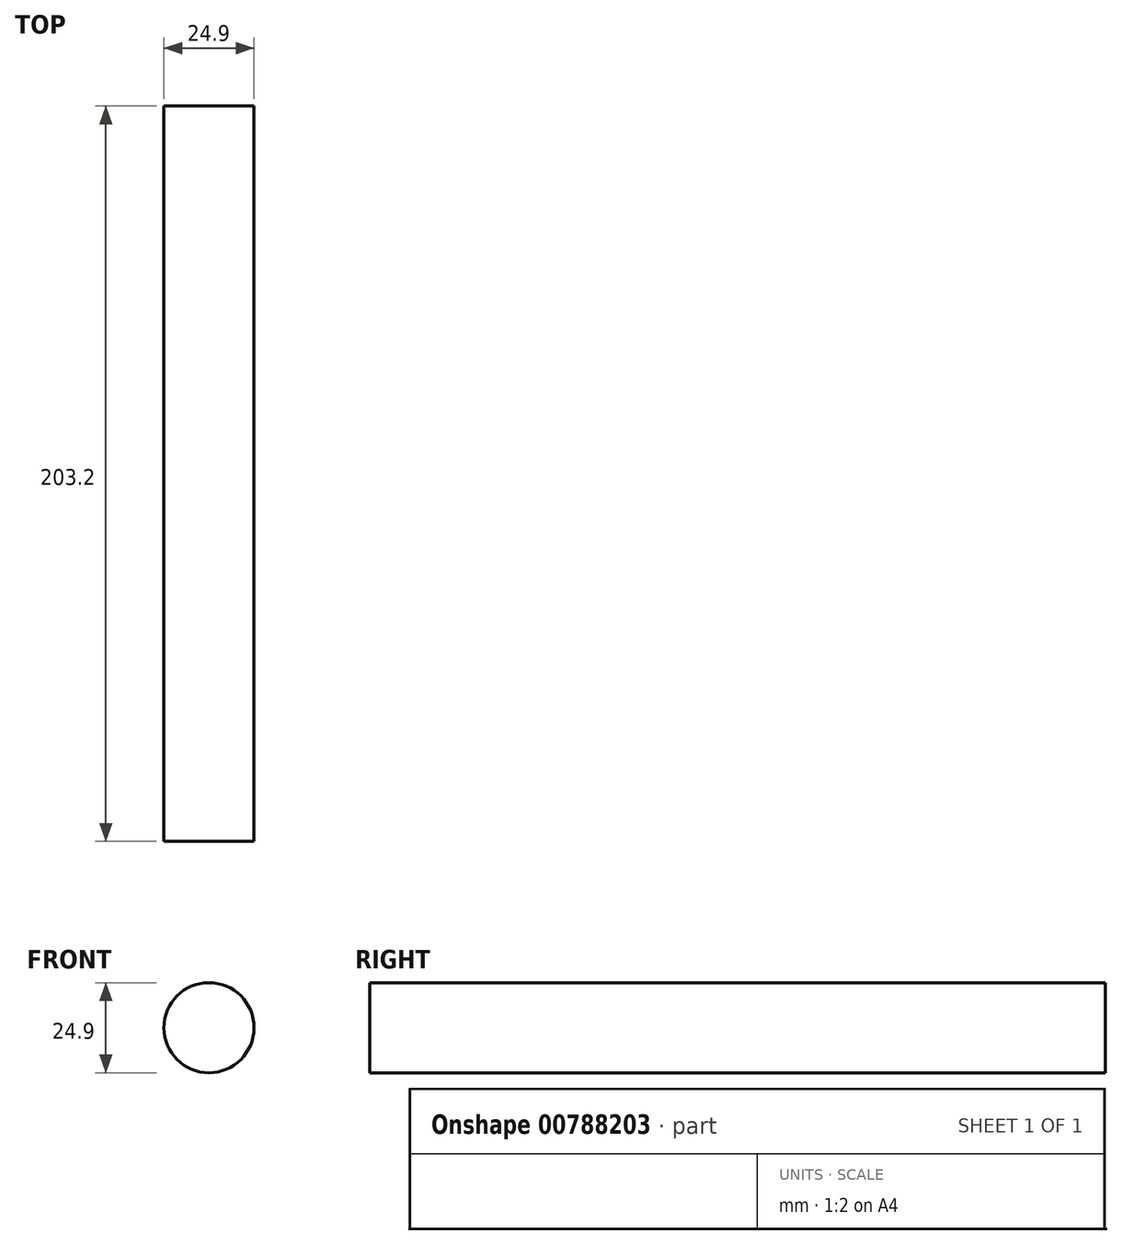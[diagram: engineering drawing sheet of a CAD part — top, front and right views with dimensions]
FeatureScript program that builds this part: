
annotation { "Feature Type Name" : "Feature", "Feature Type Description" : "" }
export const myFeature = defineFeature(function(context is Context, id is Id, definition is map)
    precondition{}
    {
        {
            var Q0;
            Q0=qCreatedBy(makeId("Front.planeOp"),FACE);
            var sketch = newSketch(context, id + "F0", { "sketchPlane" : qUnion([Q0])});
            skCircle(sketch, "E0", {"center": v(0, 0) * mm, "radius": 12.45 * mm});
            skSolve(sketch);
        }
        {
            var Q0;
            Q0=makeQuery(id+"F0.imprint","IMPRINT",FACE,{"disambiguationData":[TD([[makeQuery(id+"F0.imprint","IMPRINT",EDGE,{"derivedFrom":sQuery(id+"F0.wireOp",EDGE,"E0")}),1.0]])]});
            extrude(context, id + "F1", {"entities" : qUnion([Q0]), "depth" : 203.2 * mm, "offsetDistance" : 25.4 * mm});
        }
    });
